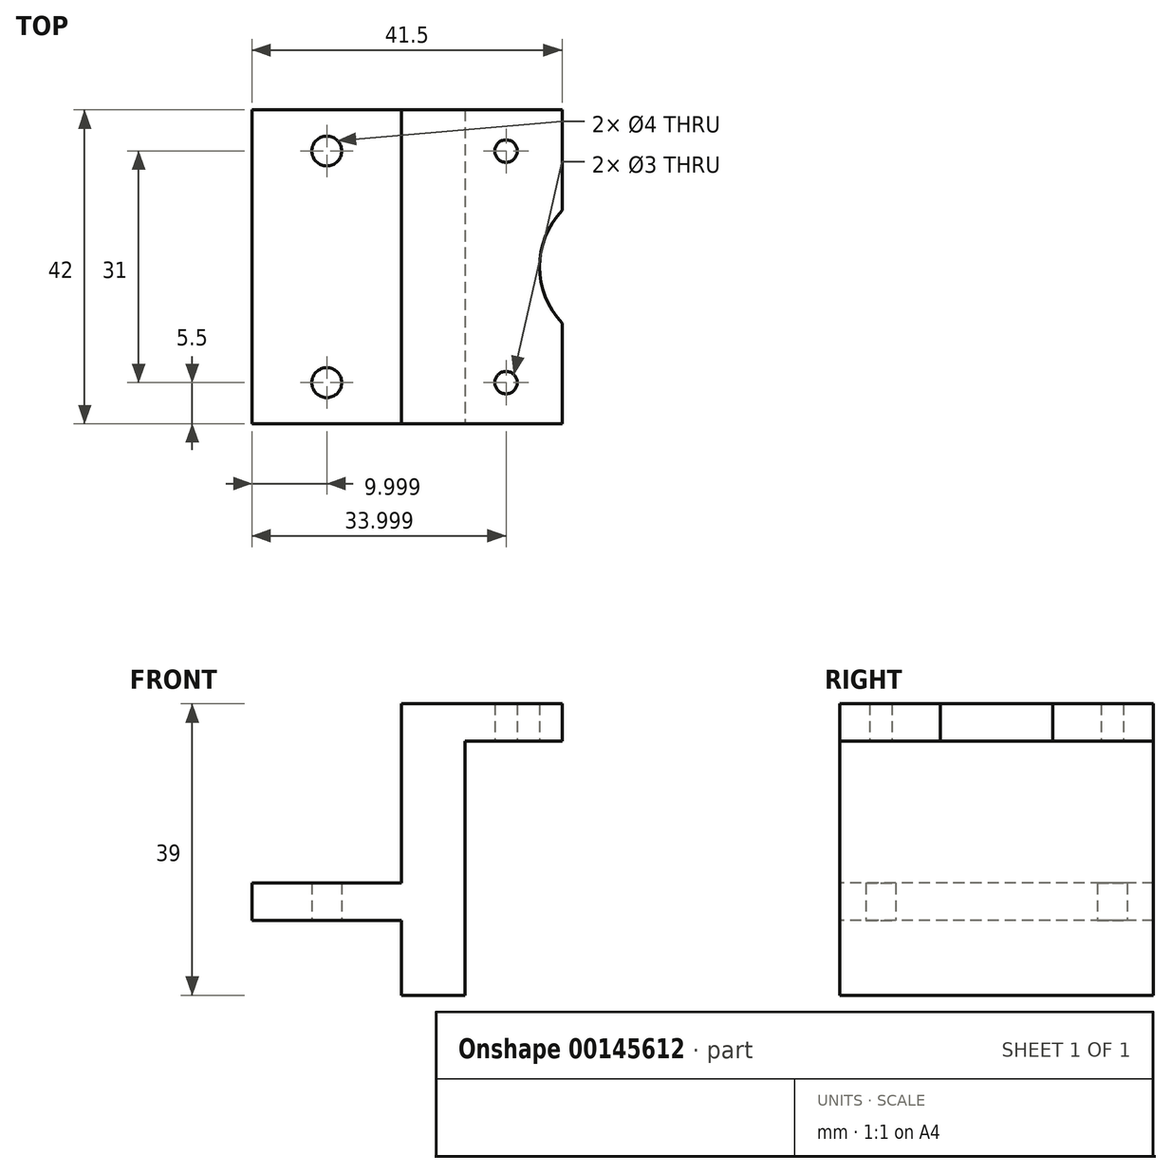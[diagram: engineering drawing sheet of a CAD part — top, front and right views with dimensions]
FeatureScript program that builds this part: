
annotation { "Feature Type Name" : "Feature", "Feature Type Description" : "" }
export const myFeature = defineFeature(function(context is Context, id is Id, definition is map)
    precondition{}
    {
        {
            var Q0;
            Q0=qCreatedBy(makeId("Top.planeOp"),FACE);
            var sketch = newSketch(context, id + "F0", { "sketchPlane" : qUnion([Q0])});
            skCircle(sketch, "E0", {"center": v(21.44, 36.5) * mm, "radius": 1.5 * mm});
            skCircle(sketch, "E1", {"center": v(21.44, 5.5) * mm, "radius": 1.5 * mm});
            skCircle(sketch, "E2", {"center": v(36.94, 21) * mm, "radius": 11 * mm});
            skLineSegment(sketch, "E3.0.3", {"start": v(15.94, 42) * mm, "end": v(15.94, 0) * mm});
            skLineSegment(sketch, "E4.0.1", {"start": v(28.94, 0) * mm, "end": v(28.94, 42) * mm});
            skLineSegment(sketch, "E5", {"start": v(15.94, 42) * mm, "end": v(28.94, 42) * mm});
            skLineSegment(sketch, "E6", {"start": v(15.94, 0) * mm, "end": v(28.94, 0) * mm});
            skPoint(sketch, "E7", {"position": v(15.94, 21) * mm});
            skPoint(sketch, "E8", {"position": v(28.94, 21) * mm});
            skLineSegment(sketch, "E9", {"start": v(15.94, 21) * mm, "end": v(36.94, 21) * mm, "construction": true});
            skLineSegment(sketch, "E10", {"start": v(15.94, 42) * mm, "end": v(-12.56, 42) * mm});
            skLineSegment(sketch, "E11", {"start": v(-12.56, 42) * mm, "end": v(-12.56, 0) * mm});
            skLineSegment(sketch, "E12", {"start": v(-12.56, 0) * mm, "end": v(15.94, 0) * mm});
            skPoint(sketch, "E13", {"position": v(-2.56, 42) * mm});
            skPoint(sketch, "E14", {"position": v(-2.56, 0) * mm});
            skLineSegment(sketch, "E15", {"start": v(-2.56, 42) * mm, "end": v(-2.56, 0) * mm, "construction": true});
            skPoint(sketch, "E16", {"position": v(-2.56, 21) * mm});
            skPoint(sketch, "E17", {"position": v(-2.56, 36.5) * mm});
            skPoint(sketch, "E18", {"position": v(-2.56, 5.5) * mm});
            skCircle(sketch, "E19", {"center": v(-2.56, 36.5) * mm, "radius": 2 * mm});
            skCircle(sketch, "E20", {"center": v(-2.56, 5.5) * mm, "radius": 2 * mm});
            skLineSegment(sketch, "E21", {"start": v(7.44, 42) * mm, "end": v(7.44, 0) * mm});
            skSolve(sketch);
        }
        {
            var Q0;
            {var subQ1=sQuery(id+"F0.wireOp",EDGE,"E11");Q0=makeQuery(id+"F0.imprint","IMPRINT",FACE,{"disambiguationData":[TD([[makeQuery(id+"F0.imprint","IMPRINT",EDGE,{"derivedFrom":subQ1}),1.0]])]});}
            extrude(context, id + "F1", {"entities" : qUnion([Q0]), "depth" : 5 * mm});
        }
        {
            var Q0;
            {var subQ0=sQuery(id+"F0.wireOp",EDGE,"E3.0.3");Q0=makeQuery(id+"F0.imprint","IMPRINT",FACE,{"disambiguationData":[TD([[makeQuery(id+"F0.imprint","IMPRINT",EDGE,{"derivedFrom":subQ0}),-1.0]])]});}
            var Q1;
            {var subQ0=sQuery(id+"F0.wireOp",EDGE,"nsZGTKym-kPXo-uJTK-MxOm-LdOrGXLxe0Ns");var subQ1=sQuery(id+"F0.wireOp",EDGE,"E21");var subQ2=makeQuery(id+"F0.imprint","INTERSECT",VERTEX,{"disambiguationData":[OD(0.0)],"derivedFrom":[subQ1,subQ0]});Q1=makeQuery(id+"F0.imprint","IMPRINT",FACE,{"disambiguationData":[TD([[makeQuery(id+"F0.imprint","IMPRINT",EDGE,{"disambiguationData":[TD([[subQ2,-1.0]])],"derivedFrom":subQ1}),1.0]])]});}
            var Q2;
            {var subQ0=sQuery(id+"F0.wireOp",EDGE,"lHjgsfWd-Oej3-HTnH-sEAT-Uk8b9eBqaBiV");var subQ1=sQuery(id+"F0.wireOp",EDGE,"E21");var subQ2=makeQuery(id+"F0.imprint","INTERSECT",VERTEX,{"disambiguationData":[OD(0.0)],"derivedFrom":[subQ1,subQ0]});Q2=makeQuery(id+"F0.imprint","IMPRINT",FACE,{"disambiguationData":[TD([[makeQuery(id+"F0.imprint","IMPRINT",EDGE,{"disambiguationData":[TD([[subQ2,-1.0]])],"derivedFrom":subQ1}),1.0]])]});}
            extrude(context, id + "F2", {"entities" : qUnion([Q0, Q1, Q2]), "operationType" : NewBodyOperationType.ADD, "depth" : (24 + 5) * mm, "hasSecondDirection" : true, "secondDirectionOppositeDirection" : true, "secondDirectionDepth" : 10 * mm});
        }
        {
            var Q0;
            Q0=makeQuery(id+"F0.imprint","IMPRINT",FACE,{"disambiguationData":[TD([[makeQuery(id+"F0.imprint","IMPRINT",EDGE,{"derivedFrom":sQuery(id+"F0.wireOp",EDGE,"E0")}),-1.0]])]});
            extrude(context, id + "F3", {"entities" : qUnion([Q0]), "operationType" : NewBodyOperationType.ADD, "depth" : (24 + 5) * mm});
        }
        {
            var Q0;
            Q0=makeQuery(id+"F0.imprint","IMPRINT",FACE,{"disambiguationData":[TD([[makeQuery(id+"F0.imprint","IMPRINT",EDGE,{"derivedFrom":sQuery(id+"F0.wireOp",EDGE,"E0")}),-1.0]])]});
            extrude(context, id + "F4", {"entities" : qUnion([Q0]), "operationType" : NewBodyOperationType.REMOVE, "depth" : 24 * mm});
        }
    });
